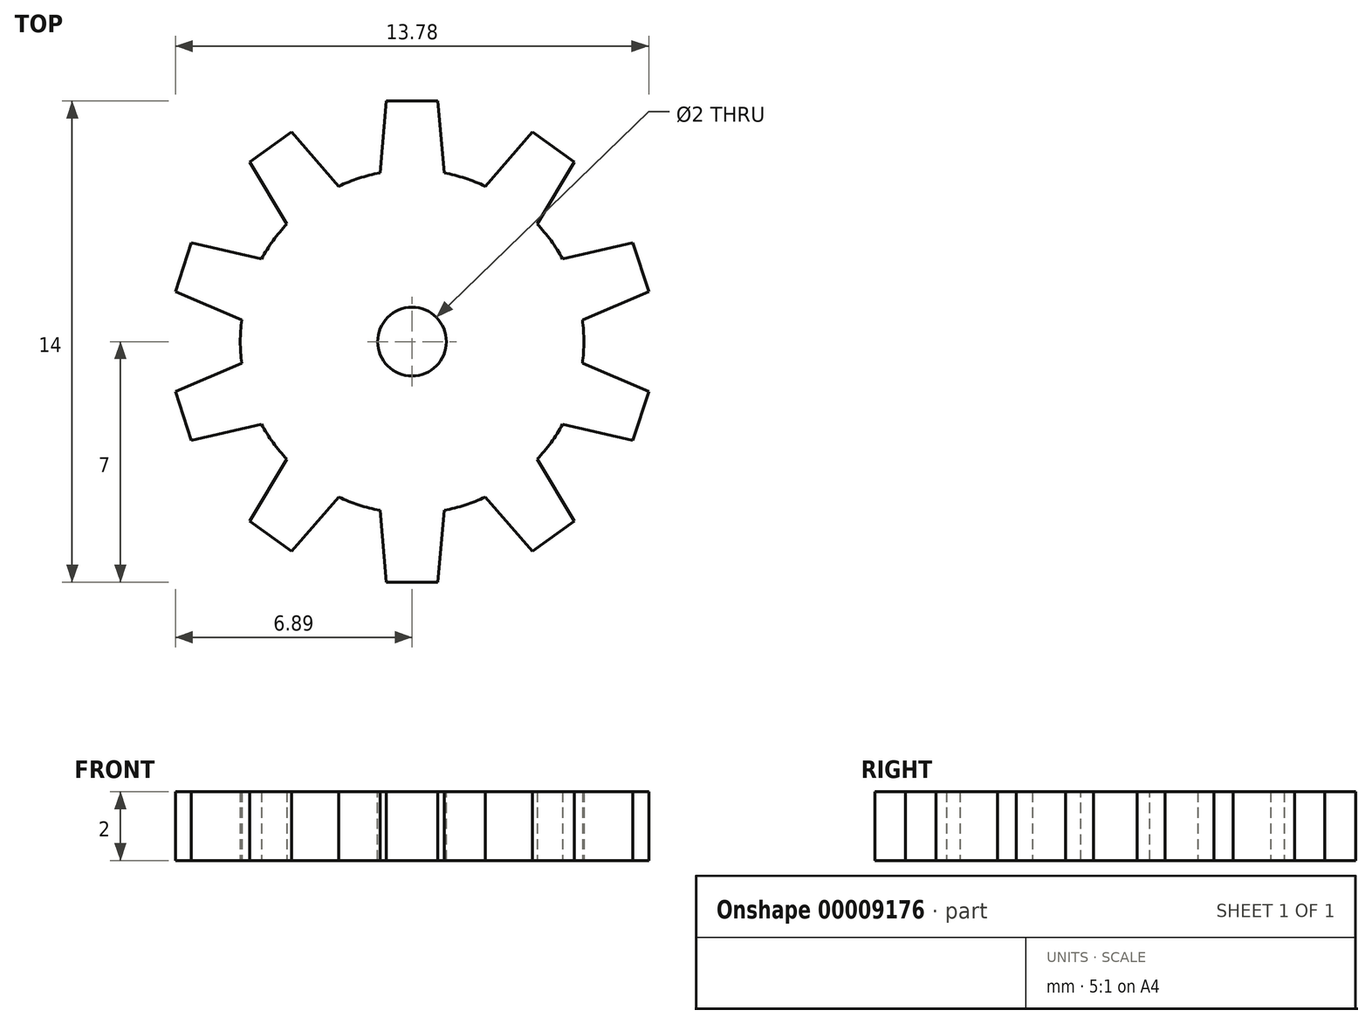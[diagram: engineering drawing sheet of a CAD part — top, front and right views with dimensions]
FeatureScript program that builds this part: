
annotation { "Feature Type Name" : "Feature", "Feature Type Description" : "" }
export const myFeature = defineFeature(function(context is Context, id is Id, definition is map)
    precondition{}
    {
        {
            var Q0;
            Q0=qCreatedBy(makeId("Top.planeOp"),FACE);
            var sketch = newSketch(context, id + "F0", { "sketchPlane" : qUnion([Q0])});
            skCircle(sketch, "E0", {"center": v(0, 0) * mm, "radius": 5 * mm});
            skLineSegment(sketch, "E1", {"start": v(0, 0) * mm, "end": v(0, 5) * mm, "construction": true});
            skLineSegment(sketch, "E2", {"start": v(-0.93, 4.91) * mm, "end": v(-0.75, 7) * mm});
            skLineSegment(sketch, "E3", {"start": v(-0.75, 7) * mm, "end": v(0, 7) * mm});
            skLineSegment(sketch, "E4.MirrorCS", {"start": v(0.93, 4.91) * mm, "end": v(0.75, 7) * mm});
            skLineSegment(sketch, "E5.MirrorCS", {"start": v(0.75, 7) * mm, "end": v(0, 7) * mm});
            skLineSegment(sketch, "E6.1.0", {"start": v(-3.64, 3.43) * mm, "end": v(-4.72, 5.22) * mm});
            skLineSegment(sketch, "E6.1.1", {"start": v(-4.72, 5.22) * mm, "end": v(-4.11, 5.66) * mm});
            skLineSegment(sketch, "E6.1.2", {"start": v(-3.5, 6.1) * mm, "end": v(-4.11, 5.66) * mm});
            skLineSegment(sketch, "E6.1.3", {"start": v(-2.13, 4.52) * mm, "end": v(-3.5, 6.1) * mm});
            skLineSegment(sketch, "E6.2.0", {"start": v(-4.96, 0.63) * mm, "end": v(-6.89, 1.45) * mm});
            skLineSegment(sketch, "E6.2.1", {"start": v(-6.89, 1.45) * mm, "end": v(-6.66, 2.16) * mm});
            skLineSegment(sketch, "E6.2.2", {"start": v(-6.43, 2.88) * mm, "end": v(-6.66, 2.16) * mm});
            skLineSegment(sketch, "E6.2.3", {"start": v(-4.38, 2.4) * mm, "end": v(-6.43, 2.88) * mm});
            skLineSegment(sketch, "E6.3.0", {"start": v(-4.38, -2.4) * mm, "end": v(-6.43, -2.88) * mm});
            skLineSegment(sketch, "E6.3.1", {"start": v(-6.43, -2.88) * mm, "end": v(-6.66, -2.16) * mm});
            skLineSegment(sketch, "E6.3.2", {"start": v(-6.89, -1.45) * mm, "end": v(-6.66, -2.16) * mm});
            skLineSegment(sketch, "E6.3.3", {"start": v(-4.96, -0.63) * mm, "end": v(-6.89, -1.45) * mm});
            skLineSegment(sketch, "E6.4.0", {"start": v(-2.13, -4.52) * mm, "end": v(-3.5, -6.1) * mm});
            skLineSegment(sketch, "E6.4.1", {"start": v(-3.5, -6.1) * mm, "end": v(-4.11, -5.66) * mm});
            skLineSegment(sketch, "E6.4.2", {"start": v(-4.72, -5.22) * mm, "end": v(-4.11, -5.66) * mm});
            skLineSegment(sketch, "E6.4.3", {"start": v(-3.64, -3.43) * mm, "end": v(-4.72, -5.22) * mm});
            skLineSegment(sketch, "E6.5.0", {"start": v(0.93, -4.91) * mm, "end": v(0.75, -7) * mm});
            skLineSegment(sketch, "E6.5.1", {"start": v(0.75, -7) * mm, "end": v(0, -7) * mm});
            skLineSegment(sketch, "E6.5.2", {"start": v(-0.75, -7) * mm, "end": v(0, -7) * mm});
            skLineSegment(sketch, "E6.5.3", {"start": v(-0.93, -4.91) * mm, "end": v(-0.75, -7) * mm});
            skLineSegment(sketch, "E6.6.0", {"start": v(3.64, -3.43) * mm, "end": v(4.72, -5.22) * mm});
            skLineSegment(sketch, "E6.6.1", {"start": v(4.72, -5.22) * mm, "end": v(4.11, -5.66) * mm});
            skLineSegment(sketch, "E6.6.2", {"start": v(3.5, -6.1) * mm, "end": v(4.11, -5.66) * mm});
            skLineSegment(sketch, "E6.6.3", {"start": v(2.13, -4.52) * mm, "end": v(3.5, -6.1) * mm});
            skLineSegment(sketch, "E6.7.0", {"start": v(4.96, -0.63) * mm, "end": v(6.89, -1.45) * mm});
            skLineSegment(sketch, "E6.7.1", {"start": v(6.89, -1.45) * mm, "end": v(6.66, -2.16) * mm});
            skLineSegment(sketch, "E6.7.2", {"start": v(6.43, -2.88) * mm, "end": v(6.66, -2.16) * mm});
            skLineSegment(sketch, "E6.7.3", {"start": v(4.38, -2.4) * mm, "end": v(6.43, -2.88) * mm});
            skLineSegment(sketch, "E6.8.0", {"start": v(4.38, 2.4) * mm, "end": v(6.43, 2.88) * mm});
            skLineSegment(sketch, "E6.8.1", {"start": v(6.43, 2.88) * mm, "end": v(6.66, 2.16) * mm});
            skLineSegment(sketch, "E6.8.2", {"start": v(6.89, 1.45) * mm, "end": v(6.66, 2.16) * mm});
            skLineSegment(sketch, "E6.8.3", {"start": v(4.96, 0.63) * mm, "end": v(6.89, 1.45) * mm});
            skLineSegment(sketch, "E6.9.0", {"start": v(2.13, 4.52) * mm, "end": v(3.5, 6.1) * mm});
            skLineSegment(sketch, "E6.9.1", {"start": v(3.5, 6.1) * mm, "end": v(4.11, 5.66) * mm});
            skLineSegment(sketch, "E6.9.2", {"start": v(4.72, 5.22) * mm, "end": v(4.11, 5.66) * mm});
            skLineSegment(sketch, "E6.9.3", {"start": v(3.64, 3.43) * mm, "end": v(4.72, 5.22) * mm});
            skSolve(sketch);
        }
        {
            var Q0;
            Q0=qSketchRegion(id+"F0",true);
            extrude(context, id + "F1", {"entities" : qUnion([Q0]), "depth" : 2 * mm});
        }
        {
            var Q0;
            Q0=makeQuery(id+"F1.opExtrude","CAP_FACE",FACE,{"disambiguationData":[OSD([sQuery(id+"F0.wireOp",EDGE,"E0"),sQuery(id+"F0.wireOp",EDGE,"E2"),sQuery(id+"F0.wireOp",EDGE,"E3"),sQuery(id+"F0.wireOp",EDGE,"E4.MirrorCS"),sQuery(id+"F0.wireOp",EDGE,"E5.MirrorCS"),sQuery(id+"F0.wireOp",EDGE,"E6.1.0"),sQuery(id+"F0.wireOp",EDGE,"E6.1.1"),sQuery(id+"F0.wireOp",EDGE,"E6.1.2"),sQuery(id+"F0.wireOp",EDGE,"E6.1.3"),sQuery(id+"F0.wireOp",EDGE,"E6.2.0"),sQuery(id+"F0.wireOp",EDGE,"E6.2.1"),sQuery(id+"F0.wireOp",EDGE,"E6.2.2"),sQuery(id+"F0.wireOp",EDGE,"E6.2.3"),sQuery(id+"F0.wireOp",EDGE,"E6.3.0"),sQuery(id+"F0.wireOp",EDGE,"E6.3.1"),sQuery(id+"F0.wireOp",EDGE,"E6.3.2"),sQuery(id+"F0.wireOp",EDGE,"E6.3.3"),sQuery(id+"F0.wireOp",EDGE,"E6.4.0"),sQuery(id+"F0.wireOp",EDGE,"E6.4.1"),sQuery(id+"F0.wireOp",EDGE,"E6.4.2"),sQuery(id+"F0.wireOp",EDGE,"E6.4.3"),sQuery(id+"F0.wireOp",EDGE,"E6.5.0"),sQuery(id+"F0.wireOp",EDGE,"E6.5.1"),sQuery(id+"F0.wireOp",EDGE,"E6.5.2"),sQuery(id+"F0.wireOp",EDGE,"E6.5.3"),sQuery(id+"F0.wireOp",EDGE,"E6.6.0"),sQuery(id+"F0.wireOp",EDGE,"E6.6.1"),sQuery(id+"F0.wireOp",EDGE,"E6.6.2"),sQuery(id+"F0.wireOp",EDGE,"E6.6.3"),sQuery(id+"F0.wireOp",EDGE,"E6.7.0"),sQuery(id+"F0.wireOp",EDGE,"E6.7.1"),sQuery(id+"F0.wireOp",EDGE,"E6.7.2"),sQuery(id+"F0.wireOp",EDGE,"E6.7.3"),sQuery(id+"F0.wireOp",EDGE,"E6.8.0"),sQuery(id+"F0.wireOp",EDGE,"E6.8.1"),sQuery(id+"F0.wireOp",EDGE,"E6.8.2"),sQuery(id+"F0.wireOp",EDGE,"E6.8.3"),sQuery(id+"F0.wireOp",EDGE,"E6.9.0"),sQuery(id+"F0.wireOp",EDGE,"E6.9.1"),sQuery(id+"F0.wireOp",EDGE,"E6.9.2"),sQuery(id+"F0.wireOp",EDGE,"E6.9.3"),sQuery(id+"F0.wireOp",EDGE,"E6.10.0"),sQuery(id+"F0.wireOp",EDGE,"E6.10.1"),sQuery(id+"F0.wireOp",EDGE,"E6.10.2"),sQuery(id+"F0.wireOp",EDGE,"E6.10.3"),sQuery(id+"F0.wireOp",EDGE,"E6.11.0"),sQuery(id+"F0.wireOp",EDGE,"E6.11.1"),sQuery(id+"F0.wireOp",EDGE,"E6.11.2"),sQuery(id+"F0.wireOp",EDGE,"E6.11.3"),sQuery(id+"F0.wireOp",EDGE,"E6.12.0"),sQuery(id+"F0.wireOp",EDGE,"E6.12.1"),sQuery(id+"F0.wireOp",EDGE,"E6.12.2"),sQuery(id+"F0.wireOp",EDGE,"E6.12.3"),sQuery(id+"F0.wireOp",EDGE,"E6.13.0"),sQuery(id+"F0.wireOp",EDGE,"E6.13.1"),sQuery(id+"F0.wireOp",EDGE,"E6.13.2"),sQuery(id+"F0.wireOp",EDGE,"E6.13.3"),sQuery(id+"F0.wireOp",EDGE,"E6.14.0"),sQuery(id+"F0.wireOp",EDGE,"E6.14.1"),sQuery(id+"F0.wireOp",EDGE,"E6.14.2"),sQuery(id+"F0.wireOp",EDGE,"E6.14.3"),sQuery(id+"F0.wireOp",EDGE,"E6.15.0"),sQuery(id+"F0.wireOp",EDGE,"E6.15.1"),sQuery(id+"F0.wireOp",EDGE,"E6.15.2"),sQuery(id+"F0.wireOp",EDGE,"E6.15.3")])],"isStart":false});
            var sketch = newSketch(context, id + "F2", { "sketchPlane" : qUnion([Q0])});
            skCircle(sketch, "E7", {"center": v(0, 0) * mm, "radius": 1 * mm});
            skSolve(sketch);
        }
        {
            var Q0;
            Q0=qSketchRegion(id+"F2",true);
            extrude(context, id + "F3", {"entities" : qUnion([Q0]), "operationType" : NewBodyOperationType.REMOVE, "endBound" : BoundingType.THROUGH_ALL, "oppositeDirection" : true, "depth" : 25 * mm});
        }
    });
